# Revit family: PRESTO ALPA 90 ARTE-V sin valvula de vaciado
name_source: partatom
category: Aparatos sanitarios
revit_build: Autodesk Revit 2015 (Build: 20140223_1515(x64)
units: mm (PartAtom-declared; Revit-internal decimal feet)

## types (1)
- 35925
    Accionamiento = Por pulsador
    CAUDAL = 8 L/Min
    CIERRE = Automático en 30 seg.
    Comentarios de tipo = Cabeza intercambiable que comprende todo el cuerpo del grifo
Apertura de pulsador de mando único con selección de temperatura mediante giro de 180º. Materiales que soportan hasta los 70ºC que permiten desinfecciones térmicas anti-legionela. Válvulas antirretorno incorporadas.
    Conexión AC = Sí
    Conexión AF = Sí
    Código de montaje = C1030220
    Descripción = Grifo temporizado mezclador de ducha para instalación vista con cuerpo de latón cromado y pulsador ARTE cromado.
    ENTRADA = Macho y hembra 3/4"
    Elevación por defecto = 1219 mm
    Fabricante = PRESTO IBÉRICA
    Imagen de tipo = <Ninguno>
    Material = LATON CROMADO
    Modelo = ALPA 90 ARTE V
    PESO BRUTO = 1.030 Kg
    REFERENCIA = 35925
    TIPO DE AGUA = Fria/Caliente
    Teléfono = (+34) 915 782 575
    URL = http://www.prestoiberica.com
